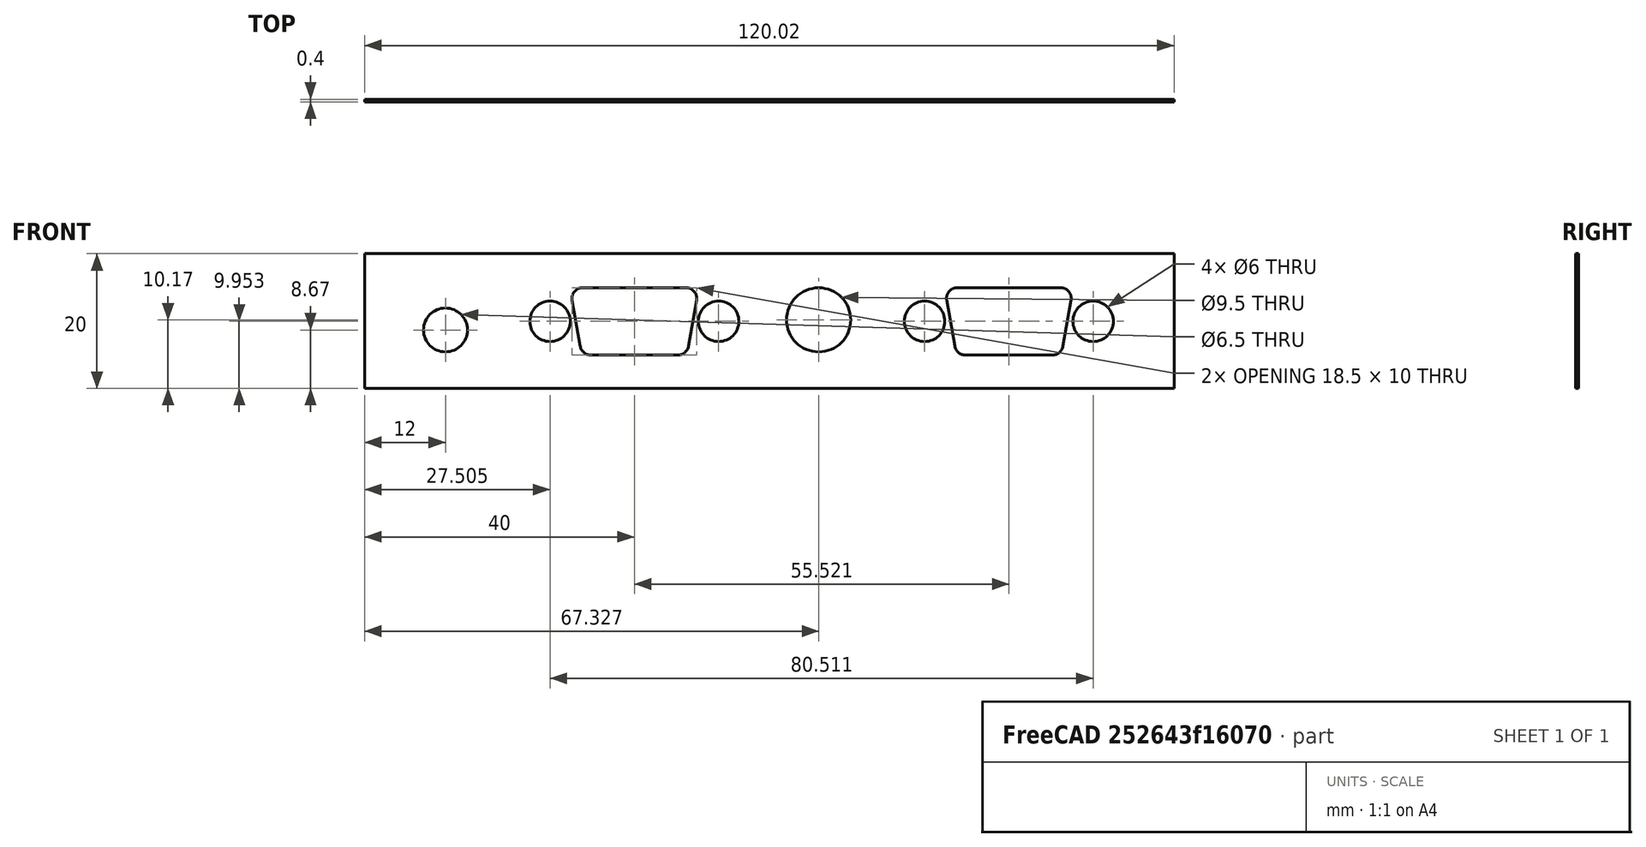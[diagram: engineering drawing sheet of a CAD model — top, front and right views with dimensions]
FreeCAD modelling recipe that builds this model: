
FCSTD DOCUMENT  (FreeCAD 0.19RUnknown)
Label: front
License: All rights reserved
LicenseURL: http://en.wikipedia.org/wiki/All_rights_reserved
objects: Sketcher::SketchObject×1, PartDesign::Pad×1, PartDesign::Body×1
note: 4 computed .brp shape members not serialized (recipe doc carries the construction recipe); baked Part::Feature solids carry a one-line shape summary decoded from their .brp

FEATURE [Sketcher::SketchObject] Sketch006  label="connector mask"
  MapMode = 5
  Placement = pos=(0,0,0) rot=(1,0,0;1.5708rad)
  Support = -> [XZ_Plane]
  sketch-geometry (40):
    g0: Circle CenterX=25 CenterY=12.67 CenterZ=0 NormalX=0 NormalY=0 NormalZ=1 AngleXU=0 Radius=3.25
    g1: LineSegment [constr] StartX=0 StartY=7.67 StartZ=0 EndX=150 EndY=7.67 EndZ=0
    g2: LineSegment [constr] StartX=0 StartY=13.9525 StartZ=0 EndX=150 EndY=13.9525 EndZ=0
    g3: Circle CenterX=40.505 CenterY=13.9525 CenterZ=0 NormalX=0 NormalY=0 NormalZ=1 AngleXU=0 Radius=3
    g4: Circle CenterX=65.495 CenterY=13.9525 CenterZ=0 NormalX=0 NormalY=0 NormalZ=1 AngleXU=0 Radius=3
    g5: LineSegment [constr] StartX=40.505 StartY=13.9525 StartZ=0 EndX=65.495 EndY=13.9525 EndZ=0
    g6: GeomPoint X=53 Y=13.9525 Z=0
    g7: LineSegment StartX=46.549 StartY=8.9525 StartZ=0 EndX=59.451 EndY=8.9525 EndZ=0
    g8: LineSegment StartX=60.65 StartY=18.9525 StartZ=0 EndX=45.35 EndY=18.9525 EndZ=0
    g9: LineSegment StartX=43.7743 StartY=17.0747 StartZ=0 EndX=44.9733 EndY=10.2747 EndZ=0
    g10: LineSegment StartX=62.2257 StartY=17.0747 StartZ=0 EndX=61.0267 EndY=10.2747 EndZ=0
    g11: ArcOfCircle CenterX=45.35 CenterY=17.3525 CenterZ=0 NormalX=0 NormalY=0 NormalZ=1 AngleXU=0 Radius=1.6 StartAngle=1.5708 EndAngle=3.31613
    g12: ArcOfCircle CenterX=46.549 CenterY=10.5525 CenterZ=0 NormalX=0 NormalY=0 NormalZ=1 AngleXU=0 Radius=1.6 StartAngle=3.31613 EndAngle=4.71239
    g13: ArcOfCircle CenterX=59.451 CenterY=10.5525 CenterZ=0 NormalX=0 NormalY=0 NormalZ=1 AngleXU=0 Radius=1.6 StartAngle=4.71239 EndAngle=6.10865
    g14: ArcOfCircle CenterX=60.65 CenterY=17.3525 CenterZ=0 NormalX=0 NormalY=0 NormalZ=1 AngleXU=0 Radius=1.6 StartAngle=6.10865 EndAngle=7.85398
    g15: LineSegment [constr] StartX=43.75 StartY=0 StartZ=0 EndX=43.75 EndY=30 EndZ=0
    g16: LineSegment [constr] StartX=62.25 StartY=0 StartZ=0 EndX=62.25 EndY=30 EndZ=0
    g17: LineSegment [constr] StartX=43.75 StartY=0 StartZ=0 EndX=62.25 EndY=0 EndZ=0
    g18: GeomPoint X=53 Y=0 Z=0
    g19: Circle CenterX=80.327 CenterY=14.17 CenterZ=0 NormalX=0 NormalY=0 NormalZ=1 AngleXU=0 Radius=4.75
    g20: Circle CenterX=96.026 CenterY=13.9525 CenterZ=0 NormalX=0 NormalY=0 NormalZ=1 AngleXU=0 Radius=3
    g21: Circle CenterX=121.016 CenterY=13.9525 CenterZ=0 NormalX=0 NormalY=0 NormalZ=1 AngleXU=0 Radius=3
    g22: LineSegment [constr] StartX=96.026 StartY=13.9525 StartZ=0 EndX=121.016 EndY=13.9525 EndZ=0
    g23: GeomPoint X=108.521 Y=13.9525 Z=0
    g24: LineSegment StartX=102.07 StartY=8.9525 StartZ=0 EndX=114.972 EndY=8.9525 EndZ=0
    g25: LineSegment StartX=116.171 StartY=18.9525 StartZ=0 EndX=100.871 EndY=18.9525 EndZ=0
    g26: LineSegment StartX=99.2953 StartY=17.0747 StartZ=0 EndX=100.494 EndY=10.2747 EndZ=0
    g27: LineSegment StartX=117.747 StartY=17.0747 StartZ=0 EndX=116.548 EndY=10.2747 EndZ=0
    g28: ArcOfCircle CenterX=100.871 CenterY=17.3525 CenterZ=0 NormalX=0 NormalY=0 NormalZ=1 AngleXU=0 Radius=1.6 StartAngle=1.5708 EndAngle=3.31613
    g29: ArcOfCircle CenterX=102.07 CenterY=10.5525 CenterZ=0 NormalX=0 NormalY=0 NormalZ=1 AngleXU=0 Radius=1.6 StartAngle=3.31613 EndAngle=4.71239
    g30: ArcOfCircle CenterX=114.972 CenterY=10.5525 CenterZ=0 NormalX=0 NormalY=0 NormalZ=1 AngleXU=0 Radius=1.6 StartAngle=4.71239 EndAngle=6.10865
    g31: ArcOfCircle CenterX=116.171 CenterY=17.3525 CenterZ=0 NormalX=0 NormalY=0 NormalZ=1 AngleXU=0 Radius=1.6 StartAngle=6.10865 EndAngle=7.85398
    g32: LineSegment [constr] StartX=99.271 StartY=0 StartZ=0 EndX=99.271 EndY=30 EndZ=0
    g33: LineSegment [constr] StartX=117.771 StartY=0 StartZ=0 EndX=117.771 EndY=30 EndZ=0
    g34: LineSegment [constr] StartX=99.271 StartY=0 StartZ=0 EndX=117.771 EndY=0 EndZ=0
    g35: GeomPoint X=108.521 Y=0 Z=0
    g36: LineSegment StartX=13 StartY=24 StartZ=0 EndX=133.016 EndY=24 EndZ=0
    g37: LineSegment StartX=133.016 StartY=24 StartZ=0 EndX=133.016 EndY=4 EndZ=0
    g38: LineSegment StartX=133.016 StartY=4 StartZ=0 EndX=13 EndY=4 EndZ=0
    g39: LineSegment StartX=13 StartY=4 StartZ=0 EndX=13 EndY=24 EndZ=0
  constraints (106):
    c: DistanceX(g-1,g0) = 25
    c: PointOnObject(g1,g-2)
    c: Horizontal(g1)
    c: DistanceX(g1,g1) = 150
    c: DistanceY(g1,g0) = 5
    c: Diameter(g0) = 6.5
    c: DistanceY(g1,g2) = 6.2825
    c: Horizontal(g2)
    c: Vertical(g2,g1)
    c: PointOnObject(g2,g-2)
    c: PointOnObject(g3,g2)
    c: Diameter(g3) = 6
    c: Equal(g3,g4) = 6
    c: PointOnObject(g4,g2)
    c: DistanceX(g3,g4) = 24.99
    c: Symmetric(g5,g5,g6)
    c: Coincident(g5,g3)
    c: Coincident(g5,g4)
    c: DistanceX(g-1,g6) = 53
    c: Horizontal(g7)
    c: Horizontal(g8)
    c: Tangent(g7,g12) = -1.5708
    c: Tangent(g9,g12) = -1.5708
    c: Tangent(g9,g11) = -1.5708
    c: Tangent(g8,g11) = -1.5708
    c: Tangent(g14,g8) = -1.5708
    c: Tangent(g14,g10) = 1.5708
    c: Tangent(g7,g13) = -1.5708
    c: Tangent(g13,g10) = 1.5708
    c: DistanceY(g6,g8) = 5
    c: DistanceY(g7,g6) = 5
    c: Radius(g11) = 1.6
    c: Equal(g11,g14)
    c: Equal(g12,g13)
    c: Equal(g13,g11)
    c: Angle(g9) = -1.39626
    c: Angle(g10) = -1.74533
    c: PointOnObject(g15,g-1)
    c: PointOnObject(g16,g-1)
    c: Vertical(g15)
    c: Vertical(g16)
    c: DistanceY(g16,g16) = 30
    c: DistanceY(g15,g15) = 30
    c: Tangent(g15,g11)
    c: Tangent(g16,g14)
    c: DistanceX(g15,g16) = 18.5
    c: Coincident(g15,g17)
    c: Symmetric(g15,g17,g18)
    c: Coincident(g17,g16)
    c: Vertical(g18,g6)
    c: DistanceY(g1,g19) = 6.5
    c: Diameter(g19) = 9.5
    c: DistanceX(g-1,g19) = 80.327
    c: Equal(g3,g20) = 6
    c: Equal(g20,g21) = 6
    c: DistanceX(g20,g21) = 24.99
    c: Symmetric(g22,g22,g23)
    c: Coincident(g22,g20)
    c: Coincident(g22,g21)
    c: Horizontal(g24)
    c: Horizontal(g25)
    c: Tangent(g24,g29) = -1.5708
    c: Tangent(g26,g29) = -1.5708
    c: Tangent(g26,g28) = -1.5708
    c: Tangent(g25,g28) = -1.5708
    c: Tangent(g31,g25) = -1.5708
    c: Tangent(g31,g27) = 1.5708
    c: Tangent(g24,g30) = -1.5708
    c: Tangent(g30,g27) = 1.5708
    c: DistanceY(g23,g25) = 5
    c: DistanceY(g24,g23) = 5
    c: Equal(g11,g28) = 1.6
    c: Equal(g28,g31)
    c: Equal(g29,g30)
    c: Equal(g30,g28)
    c: Parallel(g9,g26) = -1.39626
    c: Parallel(g10,g27) = -1.74533
    c: PointOnObject(g23,g2)
    c: PointOnObject(g20,g2)
    c: DistanceX(g-1,g23) = 108.521
    c: Coincident(g32,g34)
    c: Coincident(g33,g34)
    c: PointOnObject(g32,g-1)
    c: PointOnObject(g33,g-1)
    c: Symmetric(g32,g33,g35)
    c: Vertical(g35,g23)
    c: Vertical(g32)
    c: Vertical(g33)
    c: DistanceY(g32,g32) = 30
    c: DistanceY(g33,g33) = 30
    c: Tangent(g32,g28)
    c: Tangent(g31,g33)
    c: DistanceX(g34,g34) = 18.5
    c: DistanceY(g-1,g1) = 7.67
    c: Coincident(g36,g37)
    c: Coincident(g37,g38)
    c: Coincident(g38,g39)
    c: Coincident(g39,g36)
    c: Horizontal(g36)
    c: Horizontal(g38)
    c: Vertical(g37)
    c: Vertical(g39)
    c: DistanceY(g-1,g38) = 4
    c: DistanceY(g39,g39) = 20
    c: DistanceX(g38,g0) = 12
    c: DistanceX(g21,g37) = 12
FEATURE [PartDesign::Pad] Pad  label="connector mask pad"
  Direction = (1,1,1)
  Length = 0.4
  Length2 = 100
  Placement = pos=(0,0,0) rot=(1,0,0;1.5708rad)
  Profile = -> Sketch006
  Type = 0
FEATURE [PartDesign::Body] Body
  Group = -> [Sketch006,Pad]
  Origin = -> Origin
  Tip = -> Pad
